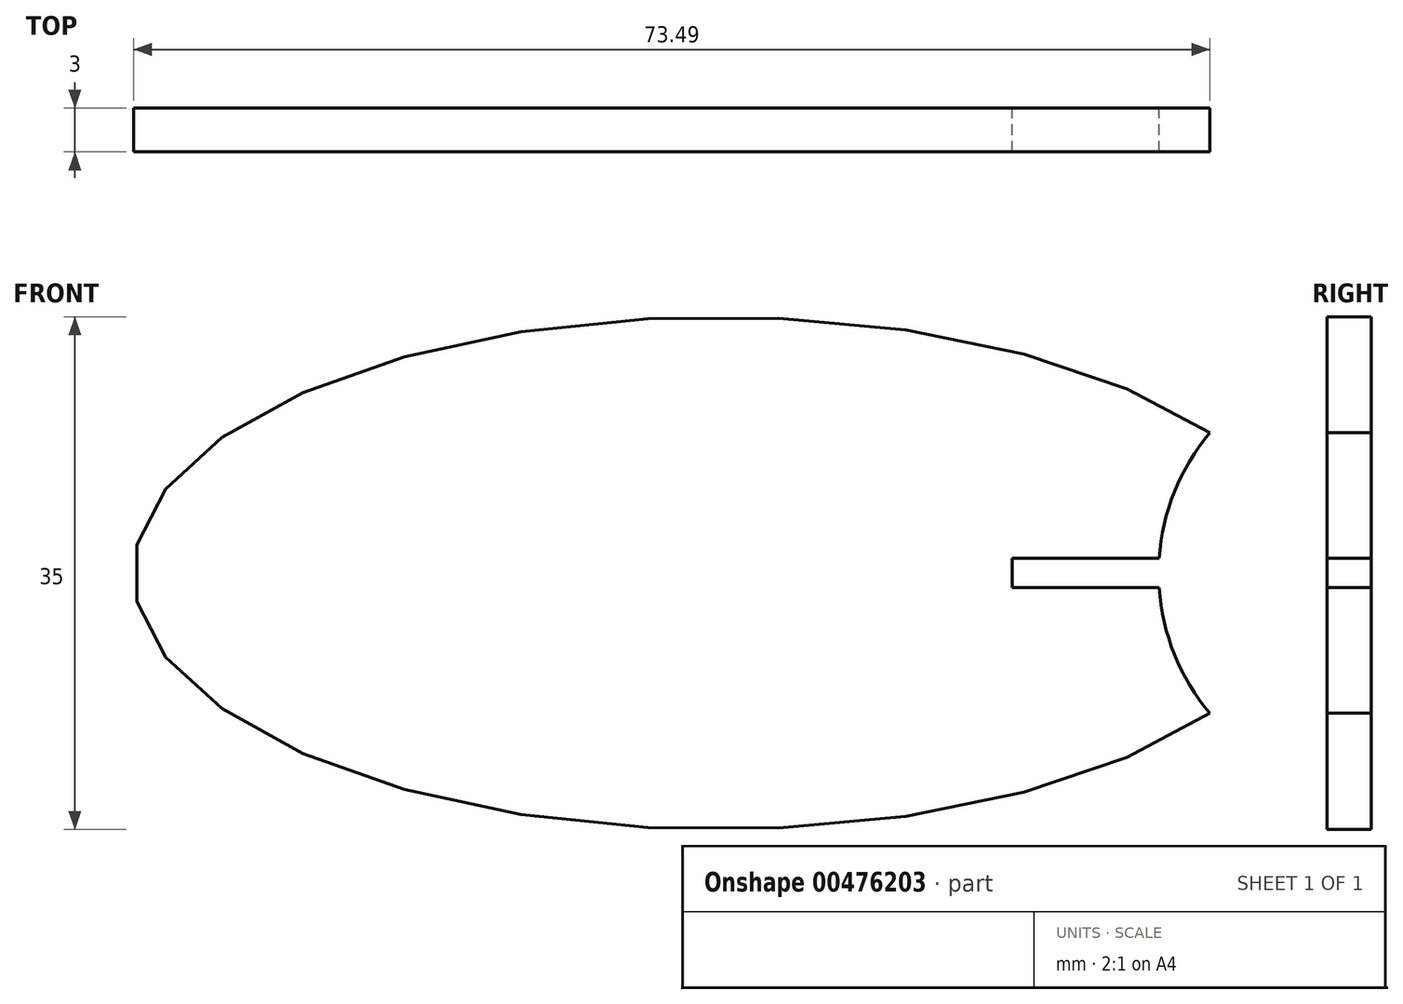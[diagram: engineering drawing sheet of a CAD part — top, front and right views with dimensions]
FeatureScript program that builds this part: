
annotation { "Feature Type Name" : "Feature", "Feature Type Description" : "" }
export const myFeature = defineFeature(function(context is Context, id is Id, definition is map)
    precondition{}
    {
        {
            var Q0;
            Q0=qCreatedBy(makeId("Front.planeOp"),FACE);
            var sketch = newSketch(context, id + "F0", { "sketchPlane" : qUnion([Q0])});
            skEllipse(sketch, "E0", {"center": v(0, 0) * mm, "majorRadius": 40 * mm, "minorRadius": 17.5 * mm, "majorAxis": v(-1, 0)});
            skSolve(sketch);
        }
        {
            var Q0;
            Q0 = qSketchRegion(id + "F0", true);
            extrude(context, id + "F1", {"entities" : qUnion([Q0]), "depth" : 3 * mm});
        }
        {
            var Q0;
            Q0=qCreatedBy(makeId("Front.planeOp"),FACE);
            var sketch = newSketch(context, id + "F2", { "sketchPlane" : qUnion([Q0])});
            skCircle(sketch, "E1", {"center": v(44.82, 0) * mm, "radius": 14.84 * mm});
            skSolve(sketch);
        }
        {
            var Q0;
            Q0 = qSketchRegion(id + "F2", true);
            extrude(context, id + "F3", {"entities" : qUnion([Q0]), "operationType" : NewBodyOperationType.REMOVE, "depth" : 25 * mm});
        }
        {
            var Q0;
            Q0=qCreatedBy(makeId("Front.planeOp"),FACE);
            var sketch = newSketch(context, id + "F4", { "sketchPlane" : qUnion([Q0])});
            skLineSegment(sketch, "E2.bottom", {"start": v(20, 1) * mm, "end": v(40, 1) * mm});
            skLineSegment(sketch, "E2.top", {"start": v(20, 0) * mm, "end": v(40, 0) * mm});
            skLineSegment(sketch, "E2.left", {"start": v(20, 1) * mm, "end": v(20, 0) * mm});
            skLineSegment(sketch, "E2.right", {"start": v(40, 1) * mm, "end": v(40, 0) * mm});
            skLineSegment(sketch, "E3.MirrorCS", {"start": v(20, -1) * mm, "end": v(40, -1) * mm});
            skLineSegment(sketch, "E4.MirrorCS", {"start": v(20, -1) * mm, "end": v(20, 0) * mm});
            skLineSegment(sketch, "E5.MirrorCS", {"start": v(40, -1) * mm, "end": v(40, 0) * mm});
            skLineSegment(sketch, "E6", {"start": v(35.47, 1) * mm, "end": v(40, 1) * mm});
            skLineSegment(sketch, "E7", {"start": v(35.49, 0) * mm, "end": v(40, 0) * mm});
            skLineSegment(sketch, "E8", {"start": v(35.49, -1) * mm, "end": v(40, -1) * mm});
            skLineSegment(sketch, "E9", {"start": v(35.47, 1) * mm, "end": v(35.49, -1) * mm});
            skSolve(sketch);
        }
        {
            var Q0;
            Q0 = qSketchRegion(id + "F4", true);
            extrude(context, id + "F5", {"entities" : qUnion([Q0]), "operationType" : NewBodyOperationType.REMOVE, "depth" : 25 * mm});
        }
    });
